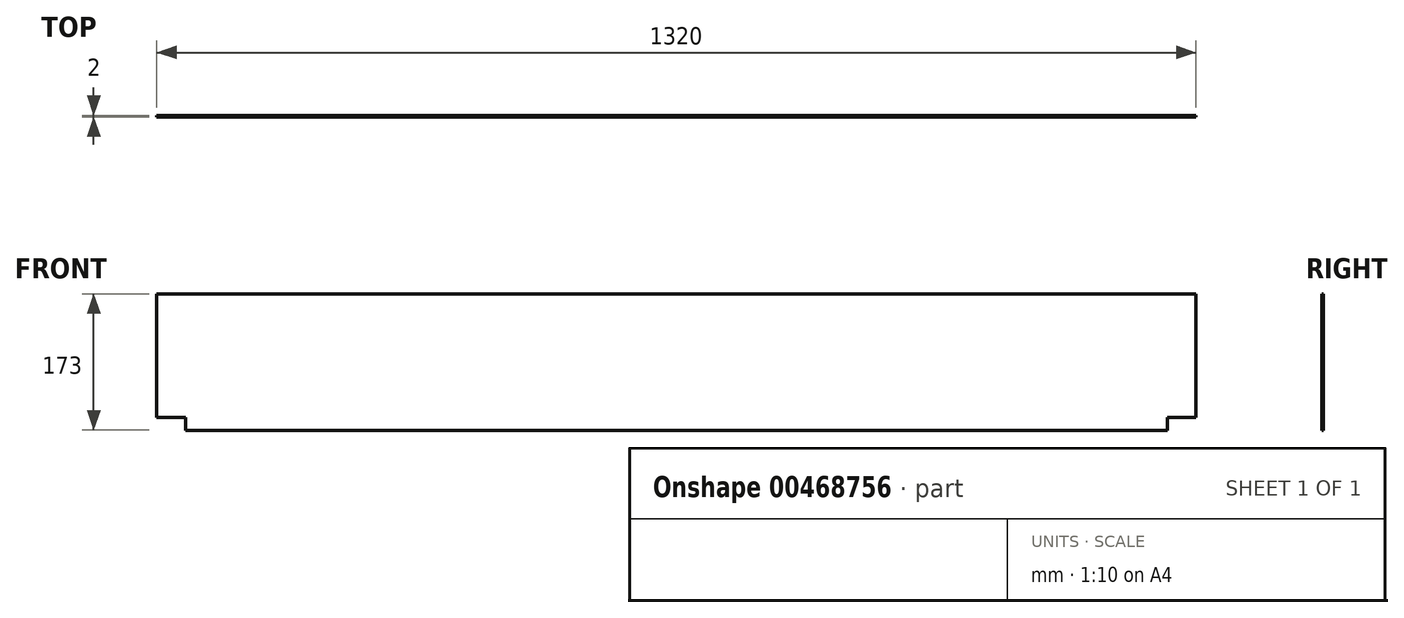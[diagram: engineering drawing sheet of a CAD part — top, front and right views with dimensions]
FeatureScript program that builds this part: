
annotation { "Feature Type Name" : "Feature", "Feature Type Description" : "" }
export const myFeature = defineFeature(function(context is Context, id is Id, definition is map)
    precondition{}
    {
        {
            var Q0;
            Q0=qCreatedBy(makeId("Front.planeOp"),FACE);
            var sketch = newSketch(context, id + "F0", { "sketchPlane" : qUnion([Q0])});
            skLineSegment(sketch, "E0.bottom", {"start": v(-391.75, 41.8) * mm, "end": v(928.25, 41.8) * mm});
            skLineSegment(sketch, "E0.top", {"start": v(-355.25, -131.2) * mm, "end": v(891.75, -131.2) * mm});
            skLineSegment(sketch, "E0.left", {"start": v(-391.75, 41.8) * mm, "end": v(-391.75, -115.2) * mm});
            skLineSegment(sketch, "E0.right", {"start": v(928.25, 41.8) * mm, "end": v(928.25, -115.2) * mm});
            skLineSegment(sketch, "E1.top", {"start": v(-391.75, -115.2) * mm, "end": v(-355.25, -115.2) * mm});
            skLineSegment(sketch, "E1.right", {"start": v(-355.25, -131.2) * mm, "end": v(-355.25, -115.2) * mm});
            skPoint(sketch, "E2.oppositeSnap0", {"position": v(-373.5, -115.2) * mm});
            skLineSegment(sketch, "E2.top", {"start": v(928.25, -115.2) * mm, "end": v(891.75, -115.2) * mm});
            skLineSegment(sketch, "E2.right", {"start": v(891.75, -131.2) * mm, "end": v(891.75, -115.2) * mm});
            skSolve(sketch);
        }
        {
            var Q0;
            Q0 = qSketchRegion(id + "F0", true);
            extrude(context, id + "F1", {"entities" : qUnion([Q0]), "depth" : 2 * mm});
        }
    });
